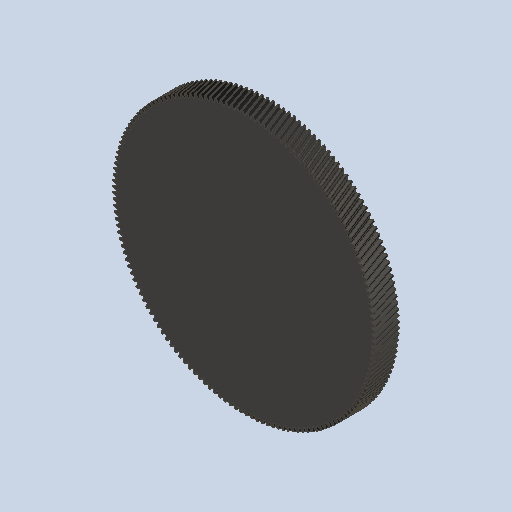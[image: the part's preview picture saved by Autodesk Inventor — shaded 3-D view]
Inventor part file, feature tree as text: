
AUTODESK INVENTOR PART (.ipt)
format: ipt  version: 2023 (Build 270158000, 158)  size: 1,773,056 bytes
history: native  units: mm (DEFAULTED — no unit token found)
features: plane x3, other x3, sketch x2, extrude x1
ambient origin geometry x8: Origin, YZ Plane, XZ Plane, XY Plane, X Axis, Y Axis, Z Axis, Center Point
bodies: Solid1 (feature_tree)
feature tree (9):
  extrude  "Extrusion1"  Depth=15.0mm TaperAngle=0.0deg
  plane  "Work Plane2"
  plane  "Work Plane8"
  plane  "Work Plane9"
  other  "Spur Gear"
  sketch  "Sketch1"  dims[d0=165.883377mm d1=15.0mm d2=0.0mm]
  sketch  "Sketch2"  dims[d3=163.883377mm d4=10.0mm d5=0.0mm d16=101.6mm d17=0.0mm d34=0.204mm d39=0.0mm d41=0.0mm d43=101.6mm d46=101.6mm d47=0.0mm d48=0.0mm]
  other  "Srf1"
  other  "Pitch Diameter"
